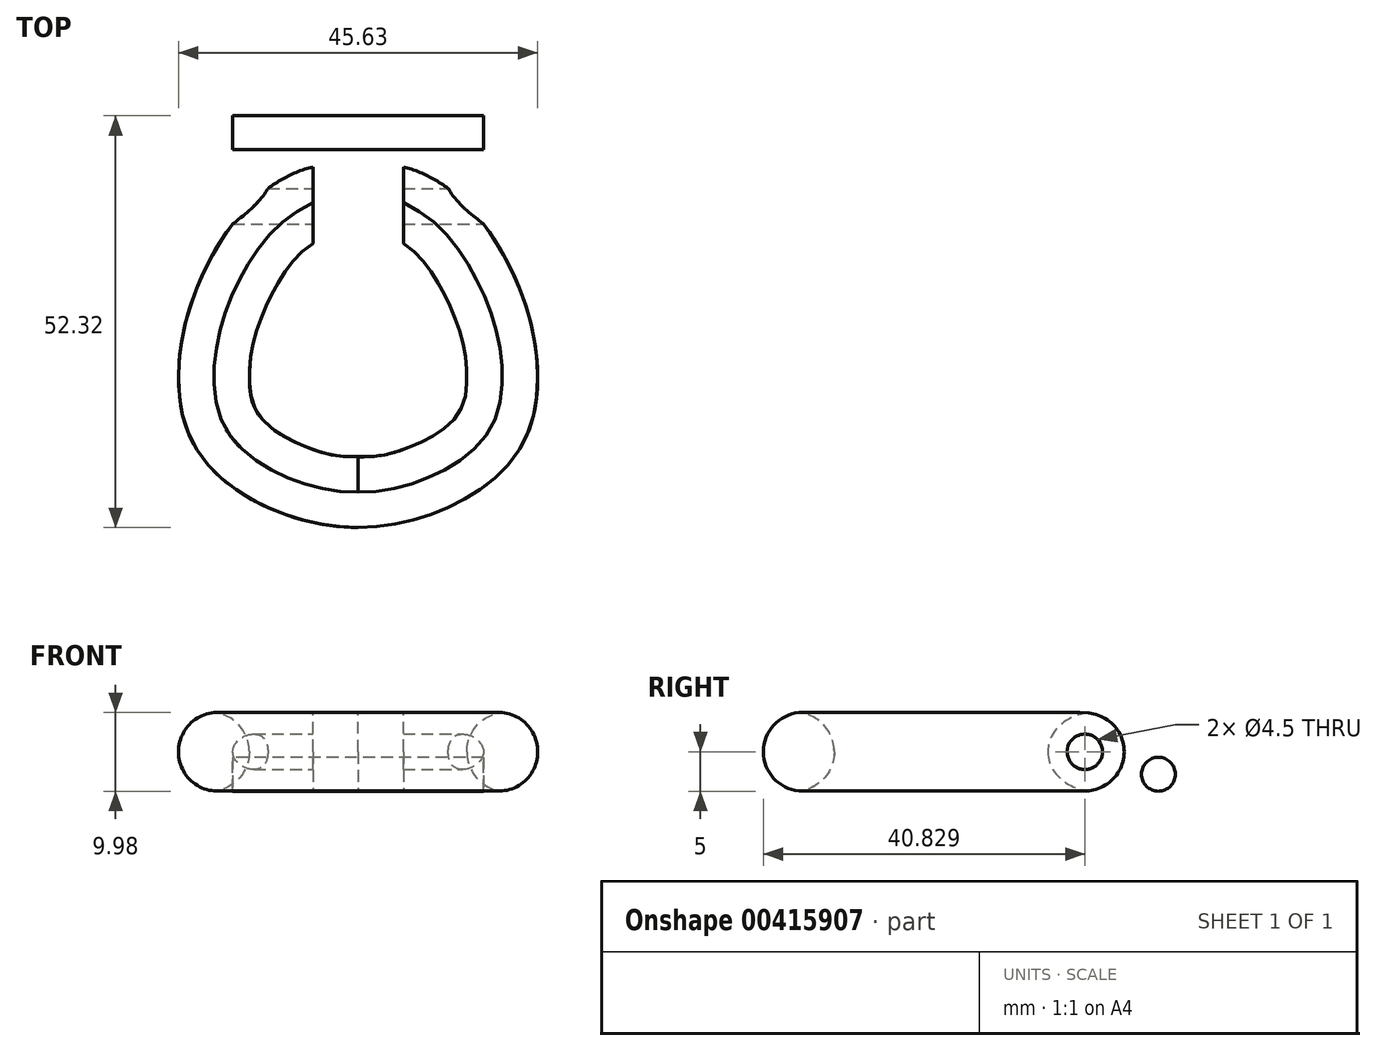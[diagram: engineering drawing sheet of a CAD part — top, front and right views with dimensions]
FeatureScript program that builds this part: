
annotation { "Feature Type Name" : "Feature", "Feature Type Description" : "" }
export const myFeature = defineFeature(function(context is Context, id is Id, definition is map)
    precondition{}
    {
        {
            var Q0;
            Q0=qCreatedBy(makeId("Top.planeOp"),FACE);
            var sketch = newSketch(context, id + "F0", { "sketchPlane" : qUnion([Q0])});
            skFitSpline(sketch, "E0", {"points": [v(-5.75, 26.7) * mm, v(-18.87, 14.8) * mm, v(-22.81, 0) * mm, v(-18.58, -11.7) * mm, v(0, -19.13) * mm], "startDerivative": vector(-69.78, -17.65) * mm, "endDerivative": vector(76.67, 0) * mm});
            skFitSpline(sketch, "E1.0", {"points": [v(-3.54, 17.97) * mm, v(-3.84, 17.9) * mm, v(-4.41, 17.7) * mm, v(-5.27, 17.28) * mm, v(-6.16, 16.69) * mm, v(-7.39, 15.65) * mm, v(-8.64, 14.23) * mm, v(-9.82, 12.52) * mm, v(-10.5, 11.35) * mm, v(-11.02, 10.38) * mm, v(-11.5, 9.41) * mm, v(-12.05, 8.2) * mm, v(-12.6, 6.77) * mm, v(-13.04, 5.36) * mm, v(-13.38, 3.98) * mm, v(-13.62, 2.65) * mm, v(-13.74, 1.57) * mm, v(-13.8, 0.73) * mm, v(-13.81, 0.12) * mm, v(-13.81, -0.48) * mm, v(-13.78, -1.22) * mm, v(-13.69, -2.05) * mm, v(-13.51, -2.9) * mm, v(-13.28, -3.6) * mm, v(-13, -4.23) * mm, v(-12.7, -4.72) * mm, v(-12.39, -5.12) * mm, v(-12.17, -5.38) * mm, v(-11.97, -5.59) * mm, v(-11.75, -5.8) * mm, v(-11.42, -6.1) * mm, v(-10.97, -6.47) * mm, v(-10.28, -6.98) * mm, v(-9.28, -7.61) * mm, v(-7.9, -8.33) * mm, v(-5.87, -9.16) * mm, v(-3.13, -9.92) * mm, v(-1, -10.13) * mm, v(0, -10.13) * mm]});
            skLineSegment(sketch, "E2", {"start": v(-5.75, 26.7) * mm, "end": v(-5.75, 16.96) * mm});
            skFitSpline(sketch, "E3.MirrorCS", {"points": [v(5.75, 26.7) * mm, v(18.87, 14.8) * mm, v(22.81, 0) * mm, v(18.58, -11.7) * mm, v(0, -19.13) * mm], "startDerivative": vector(69.78, -17.65) * mm, "endDerivative": vector(-76.67, 0) * mm});
            skLineSegment(sketch, "E4.MirrorCS", {"start": v(5.75, 26.7) * mm, "end": v(5.75, 16.96) * mm});
            skLineSegment(sketch, "E5", {"start": v(0, -19.13) * mm, "end": v(-7.1, -19.13) * mm, "construction": true});
            skFitSpline(sketch, "E6.0", {"points": [v(3.54, 17.97) * mm, v(3.84, 17.9) * mm, v(4.41, 17.7) * mm, v(5.27, 17.28) * mm, v(6.16, 16.69) * mm, v(7.39, 15.65) * mm, v(8.64, 14.23) * mm, v(9.82, 12.52) * mm, v(10.5, 11.35) * mm, v(11.02, 10.38) * mm, v(11.5, 9.41) * mm, v(12.05, 8.2) * mm, v(12.6, 6.77) * mm, v(13.04, 5.36) * mm, v(13.38, 3.98) * mm, v(13.62, 2.65) * mm, v(13.74, 1.57) * mm, v(13.8, 0.73) * mm, v(13.81, 0.12) * mm, v(13.81, -0.48) * mm, v(13.78, -1.22) * mm, v(13.69, -2.05) * mm, v(13.51, -2.9) * mm, v(13.28, -3.6) * mm, v(13, -4.23) * mm, v(12.7, -4.72) * mm, v(12.39, -5.12) * mm, v(12.17, -5.38) * mm, v(11.97, -5.59) * mm, v(11.75, -5.8) * mm, v(11.42, -6.1) * mm, v(10.97, -6.47) * mm, v(10.28, -6.98) * mm, v(9.28, -7.61) * mm, v(7.9, -8.33) * mm, v(5.87, -9.16) * mm, v(3.13, -9.92) * mm, v(1, -10.13) * mm, v(0, -10.13) * mm], "construction": true});
            skPoint(sketch, "E7", {"position": v(5.75, 16.96) * mm});
            skFitSpline(sketch, "E8", {"points": [v(3.54, 17.97) * mm, v(3.84, 17.9) * mm, v(4.41, 17.7) * mm, v(5.27, 17.28) * mm, v(6.16, 16.69) * mm, v(7.39, 15.65) * mm, v(8.64, 14.23) * mm, v(9.82, 12.52) * mm, v(10.5, 11.35) * mm, v(11.02, 10.38) * mm, v(11.5, 9.41) * mm, v(12.05, 8.2) * mm, v(12.6, 6.77) * mm, v(13.04, 5.36) * mm, v(13.38, 3.98) * mm, v(13.62, 2.65) * mm, v(13.74, 1.57) * mm, v(13.8, 0.73) * mm, v(13.81, 0.12) * mm, v(13.81, -0.48) * mm, v(13.78, -1.22) * mm, v(13.69, -2.05) * mm, v(13.51, -2.9) * mm, v(13.28, -3.6) * mm, v(13, -4.23) * mm, v(12.7, -4.72) * mm, v(12.39, -5.12) * mm, v(12.17, -5.38) * mm, v(11.97, -5.59) * mm, v(11.75, -5.8) * mm, v(11.42, -6.1) * mm, v(10.97, -6.47) * mm, v(10.28, -6.98) * mm, v(9.28, -7.61) * mm, v(7.9, -8.33) * mm, v(5.87, -9.16) * mm, v(3.13, -9.92) * mm, v(1, -10.13) * mm, v(0, -10.13) * mm]});
            skLineSegment(sketch, "E9", {"start": v(0, -10.13) * mm, "end": v(-0.16, -10.13) * mm});
            skSolve(sketch);
        }
        {
            var Q0;
            Q0=qSketchRegion(id+"F0",true);
            extrude(context, id + "F1", {"entities" : qUnion([Q0]), "depth" : 10 * mm});
        }
        {
            var Q0;
            Q0=makeQuery(id+"F1.opExtrude","SWEPT_FACE",FACE,{"disambiguationData":[OSD([sQuery(id+"F0.wireOp",EDGE,"E2")])]});
            var sketch = newSketch(context, id + "F2", { "sketchPlane" : qUnion([Q0])});
            skCircle(sketch, "E10", {"center": v(21.7, 5) * mm, "radius": 2.25 * mm});
            skSolve(sketch);
        }
        {
            var Q0;
            Q0=makeQuery(id+"F1.opExtrude","CAP_EDGE",EDGE,{"disambiguationData":[OSD([sQuery(id+"F0.wireOp",EDGE,"E1.0")])],"isStart":true});
            var Q1;
            Q1=makeQuery(id+"F1.opExtrude","CAP_EDGE",EDGE,{"disambiguationData":[OSD([sQuery(id+"F0.wireOp",EDGE,"E9")])],"isStart":true});
            var Q2;
            Q2=makeQuery(id+"F1.opExtrude","CAP_EDGE",EDGE,{"disambiguationData":[OSD([sQuery(id+"F0.wireOp",EDGE,"E1.0")])],"isStart":false});
            var Q3;
            Q3=makeQuery(id+"F1.opExtrude","CAP_EDGE",EDGE,{"disambiguationData":[OSD([sQuery(id+"F0.wireOp",EDGE,"E9")])],"isStart":false});
            var Q4;
            Q4=makeQuery(id+"F1.opExtrude","CAP_EDGE",EDGE,{"disambiguationData":[OSD([sQuery(id+"F0.wireOp",EDGE,"E8")])],"isStart":false});
            var Q5;
            Q5=makeQuery(id+"F1.opExtrude","CAP_EDGE",EDGE,{"disambiguationData":[OSD([sQuery(id+"F0.wireOp",EDGE,"E8")])],"isStart":true});
            var Q6;
            Q6=makeQuery(id+"F1.opExtrude","CAP_EDGE",EDGE,{"disambiguationData":[OSD([sQuery(id+"F0.wireOp",EDGE,"E3.MirrorCS")])],"isStart":true});
            var Q7;
            Q7=makeQuery(id+"F1.opExtrude","CAP_EDGE",EDGE,{"disambiguationData":[OSD([sQuery(id+"F0.wireOp",EDGE,"E3.MirrorCS")])],"isStart":false});
            var Q8;
            Q8=makeQuery(id+"F1.opExtrude","CAP_EDGE",EDGE,{"disambiguationData":[OSD([sQuery(id+"F0.wireOp",EDGE,"E0")])],"isStart":false});
            var Q9;
            Q9=makeQuery(id+"F1.opExtrude","CAP_EDGE",EDGE,{"disambiguationData":[OSD([sQuery(id+"F0.wireOp",EDGE,"E0")])],"isStart":true});
            fillet(context, id + "F3", {"entities" : qUnion([Q0, Q1, Q2, Q3, Q4, Q5, Q6, Q7, Q8, Q9]), "radius" : 5 * mm, "tangentPropagation" : true, "allowEdgeOverflow" : false});
        }
        {
            var Q0;
            Q0 = qSketchRegion(id + "F2", true);
            extrude(context, id + "F4", {"entities" : qUnion([Q0]), "operationType" : NewBodyOperationType.REMOVE, "endBound" : BoundingType.THROUGH_ALL, "oppositeDirection" : true, "depth" : 25 * mm, "hasSecondDirection" : true, "secondDirectionBound" : SecondDirectionBoundingType.THROUGH_ALL, "secondDirectionOppositeDirection" : false, "secondDirectionDepth" : 25 * mm});
        }
        {
            var Q0;
            Q0=qCreatedBy(makeId("Right.planeOp"),FACE);
            var sketch = newSketch(context, id + "F5", { "sketchPlane" : qUnion([Q0])});
            skCircle(sketch, "E11", {"center": v(31.04, 2.15) * mm, "radius": 2.15 * mm});
            skSolve(sketch);
        }
        {
            var Q0;
            Q0=makeQuery(id+"F5.imprint","IMPRINT",FACE,{"disambiguationData":[TD([[makeQuery(id+"F5.imprint","IMPRINT",EDGE,{"derivedFrom":sQuery(id+"F5.wireOp",EDGE,"E11")}),1.0]])]});
            extrude(context, id + "F6", {"entities" : qUnion([Q0]), "depth" : 15.92 * mm, "hasSecondDirection" : true, "secondDirectionOppositeDirection" : true, "secondDirectionDepth" : 15.92 * mm});
        }
    });
